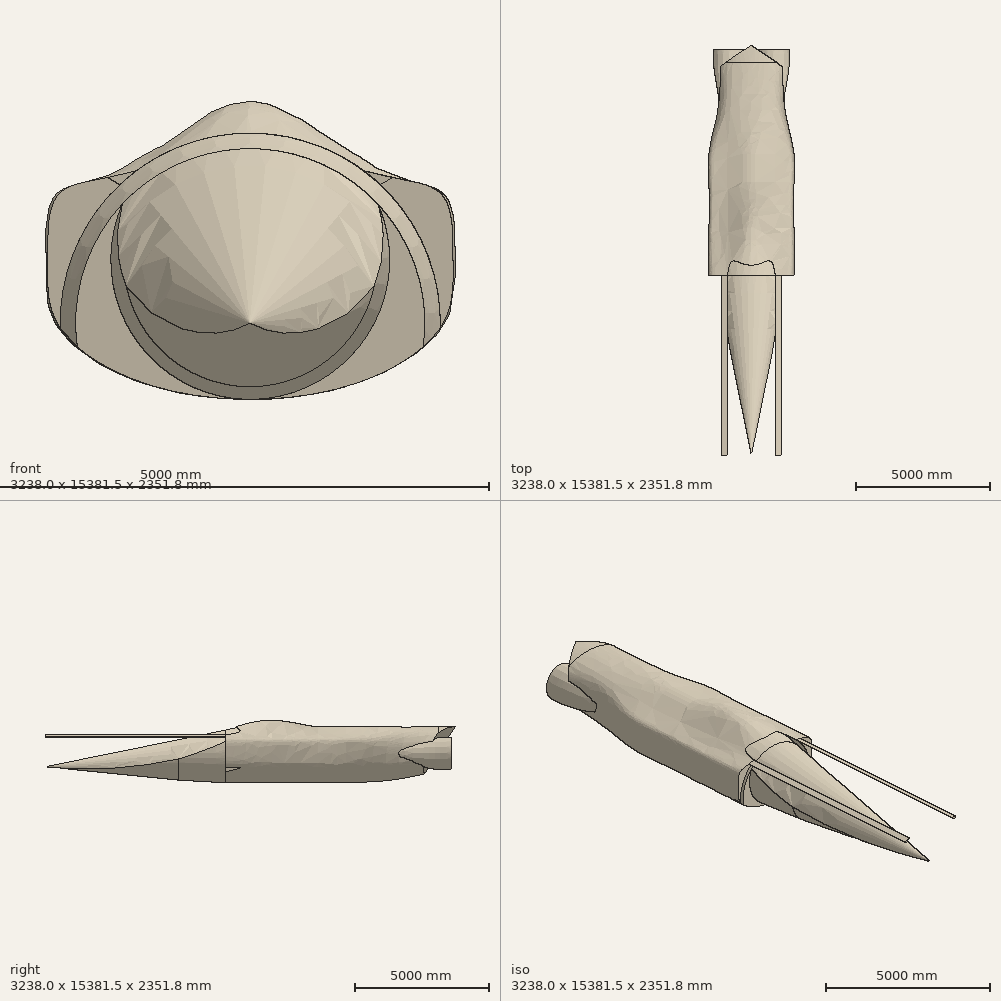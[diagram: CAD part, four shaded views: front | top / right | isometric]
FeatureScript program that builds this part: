
annotation { "Feature Type Name" : "Feature", "Feature Type Description" : "" }
export const myFeature = defineFeature(function(context is Context, id is Id, definition is map)
    precondition{}
    {
        {
            var Q0;
            Q0=qCreatedBy(makeId("Front.planeOp"),FACE);
            cPlane(context, id + "F0", {"entities" : qUnion([Q0]), "cplaneType" : CPlaneType.OFFSET, "offset" : 1750 * mm, "width" : 152.4 * mm, "height" : 152.4 * mm});
        }
        {
            var Q0;
            Q0=qCreatedBy(id+"F0.planeOp",FACE);
            var sketch = newSketch(context, id + "F1", { "sketchPlane" : qUnion([Q0])});
            skPoint(sketch, "E0.middle", {"position": v(0, 0) * mm});
            skFitSpline(sketch, "E1", {"points": [v(0, 877.87) * mm, v(1060, 662.5) * mm, v(1517.6, 506.84) * mm, v(1600, 0) * mm, v(1517.6, -506.84) * mm, v(750, -1000) * mm, v(-750, -1000) * mm, v(-1517.6, -506.84) * mm, v(-1600, 0) * mm, v(-1517.6, 506.84) * mm, v(-1060, 662.5) * mm, v(0, 877.87) * mm]});
            skSolve(sketch);
        }
        {
            var Q0;
            Q0=qCreatedBy(makeId("Front.planeOp"),FACE);
            var sketch = newSketch(context, id + "F2", { "sketchPlane" : qUnion([Q0])});
            skPoint(sketch, "E2.middle", {"position": v(0, 0) * mm});
            skFitSpline(sketch, "E3", {"points": [v(0, 1250) * mm, v(1060, 662.5) * mm, v(1517.6, 506.84) * mm, v(1600, 0) * mm, v(1517.6, -506.84) * mm, v(750, -1000) * mm, v(-750, -1000) * mm, v(-1517.6, -506.84) * mm, v(-1600, 0) * mm, v(-1517.6, 506.84) * mm, v(-1060, 662.5) * mm, v(0, 1250) * mm]});
            skSolve(sketch);
        }
        {
            var Q0;
            Q0=qCreatedBy(makeId("Front.planeOp"),FACE);
            cPlane(context, id + "F3", {"entities" : qUnion([Q0]), "cplaneType" : CPlaneType.OFFSET, "offset" : 1750 * mm, "oppositeDirection" : true, "width" : 150 * mm, "height" : 150 * mm});
        }
        {
            var Q0;
            Q0=qCreatedBy(id+"F3.planeOp",FACE);
            var sketch = newSketch(context, id + "F4", { "sketchPlane" : qUnion([Q0])});
            skPoint(sketch, "E4.middle", {"position": v(0, 0) * mm});
            skFitSpline(sketch, "E5", {"points": [v(0, 1000) * mm, v(1060, 662.5) * mm, v(1517.6, 506.84) * mm, v(1600, 0) * mm, v(1517.6, -506.84) * mm, v(750, -1000) * mm, v(-750, -1000) * mm, v(-1517.6, -506.84) * mm, v(-1600, 0) * mm, v(-1517.6, 506.84) * mm, v(-1060, 662.5) * mm, v(0, 1000) * mm]});
            skSolve(sketch);
        }
        {
            var Q0;
            Q0=qCreatedBy(makeId("Front.planeOp"),FACE);
            cPlane(context, id + "F5", {"entities" : qUnion([Q0]), "cplaneType" : CPlaneType.OFFSET, "offset" : 2800 * mm, "oppositeDirection" : true, "width" : 150 * mm, "height" : 150 * mm});
        }
        {
            var Q0;
            Q0=qCreatedBy(id+"F5.planeOp",FACE);
            var sketch = newSketch(context, id + "F6", { "sketchPlane" : qUnion([Q0])});
            skPoint(sketch, "E6.middle", {"position": v(0, 0) * mm});
            skFitSpline(sketch, "E7", {"points": [v(0, 1000) * mm, v(1060, 662.5) * mm, v(1517.6, 506.84) * mm, v(1600, 0) * mm, v(1517.6, -506.84) * mm, v(750, -1000) * mm, v(-750, -1000) * mm, v(-1517.6, -506.84) * mm, v(-1600, 0) * mm, v(-1517.6, 506.84) * mm, v(-1060, 662.5) * mm, v(0, 1000) * mm]});
            skSolve(sketch);
        }
        {
            var Q0;
            Q0=qCreatedBy(makeId("Front.planeOp"),FACE);
            cPlane(context, id + "F7", {"entities" : qUnion([Q0]), "cplaneType" : CPlaneType.OFFSET, "offset" : 4500 * mm, "oppositeDirection" : true, "width" : 150 * mm, "height" : 150 * mm});
        }
        {
            var Q0;
            Q0=qCreatedBy(id+"F7.planeOp",FACE);
            var sketch = newSketch(context, id + "F8", { "sketchPlane" : qUnion([Q0])});
            skPoint(sketch, "E8.middle", {"position": v(0, 0) * mm});
            skFitSpline(sketch, "E9", {"points": [v(0, 1000) * mm, v(1060, 662.5) * mm, v(1250, 0) * mm, v(1060, -662.5) * mm, v(0, -1000) * mm, v(-1060, -662.5) * mm, v(-1250, 0) * mm, v(-1060, 662.5) * mm, v(0, 1000) * mm]});
            skSolve(sketch);
        }
        {
            var Q0;
            Q0=qCreatedBy(makeId("Front.planeOp"),FACE);
            cPlane(context, id + "F9", {"entities" : qUnion([Q0]), "cplaneType" : CPlaneType.OFFSET, "offset" : 6232.05 * mm, "oppositeDirection" : true, "width" : 150 * mm, "height" : 150 * mm});
        }
        {
            var Q0;
            Q0=qCreatedBy(id+"F9.planeOp",FACE);
            var sketch = newSketch(context, id + "F10", { "sketchPlane" : qUnion([Q0])});
            skPoint(sketch, "E10.middle", {"position": v(0, 0) * mm});
            skFitSpline(sketch, "E11", {"points": [v(0, 1000) * mm, v(1060, 662.5) * mm, v(1250, 0) * mm, v(848, -530) * mm, v(-848, -530) * mm, v(-1250, 0) * mm, v(-1060, 662.5) * mm, v(0, 1000) * mm]});
            skSolve(sketch);
        }
        {
            var Q0;
            Q0 = qSketchRegion(id + "F1", true);
            var Q1;
            Q1 = qSketchRegion(id + "F2", true);
            var Q2;
            Q2 = qSketchRegion(id + "F4", true);
            var Q3;
            Q3 = qSketchRegion(id + "F6", true);
            var Q4;
            Q4 = qSketchRegion(id + "F8", true);
            var Q5;
            Q5 = qSketchRegion(id + "F10", true);
            loft(context, id + "F11", {"sheetProfilesArray" : [{ "sheetProfileEntities" : qUnion([Q0]) }, { "sheetProfileEntities" : qUnion([Q1]) }, { "sheetProfileEntities" : qUnion([Q2]) }, { "sheetProfileEntities" : qUnion([Q3]) }, { "sheetProfileEntities" : qUnion([Q4]) }, { "sheetProfileEntities" : qUnion([Q5]) }]});
        }
        {
            var Q0;
            Q0=makeQuery(id+"F11.opLoft","CAP_FACE",FACE,{"disambiguationData":[OSD([makeQuery(id+"F10.imprint","IMPRINT",FACE,{"disambiguationData":[TD([[makeQuery(id+"F10.imprint","IMPRINT",EDGE,{"derivedFrom":sQuery(id+"F10.wireOp",EDGE,"E11")}),-1.0]])]})])],"isStart":true});
            extrude(context, id + "F12", {"entities" : qUnion([Q0]), "operationType" : NewBodyOperationType.ADD, "depth" : 649.4 * mm});
        }
        {
            var Q0;
            Q0=qCreatedBy(makeId("Right.planeOp"),FACE);
            var sketch = newSketch(context, id + "F13", { "sketchPlane" : qUnion([Q0])});
            skLineSegment(sketch, "E12", {"start": v(0, 0) * mm, "end": v(4500, 0) * mm});
            skLineSegment(sketch, "E13", {"start": v(4500, 0) * mm, "end": v(6232.05, 0) * mm});
            skLineSegment(sketch, "E14", {"start": v(4500, 0) * mm, "end": v(4500, 1000) * mm});
            skLineSegment(sketch, "E15", {"start": v(4500, 1000) * mm, "end": v(6881.46, 1000) * mm});
            skLineSegment(sketch, "E16", {"start": v(6881.46, 1000) * mm, "end": v(6881.46, -1000) * mm});
            skLineSegment(sketch, "E17", {"start": v(6881.46, 1000) * mm, "end": v(6232.05, 0) * mm});
            skLineSegment(sketch, "E18", {"start": v(6232.05, 0) * mm, "end": v(5582.64, -1000) * mm});
            skLineSegment(sketch, "E19", {"start": v(5582.64, -1000) * mm, "end": v(6881.46, -1000) * mm});
            skSolve(sketch);
        }
        {
            var Q0;
            Q0=makeQuery(id+"F13.imprint","IMPRINT",FACE,{"disambiguationData":[TD([[makeQuery(id+"F13.imprint","IMPRINT",EDGE,{"derivedFrom":sQuery(id+"F13.wireOp",EDGE,"E16")}),-1.0]])]});
            var Q1;
            Q1=sQuery(id+"F13.wireOp",EDGE,"E15");
            revolve(context, id + "F14", {"operationType" : NewBodyOperationType.REMOVE, "entities" : qUnion([Q0]), "axis" : qUnion([Q1]), "revolveType" : RevolveType.SYMMETRIC, "oppositeDirection" : true, "angle" : 182 * degree});
        }
        {
            var Q0;
            Q0=makeQuery(id+"F11.opLoft","CAP_FACE",FACE,{"disambiguationData":[OSD([makeQuery(id+"F1.imprint","IMPRINT",FACE,{"disambiguationData":[TD([[makeQuery(id+"F1.imprint","IMPRINT",EDGE,{"derivedFrom":sQuery(id+"F1.wireOp",EDGE,"E1")}),-1.0]])]})])],"isStart":true});
            extrude(context, id + "F15", {"entities" : qUnion([Q0]), "depth" : 6750 * mm});
        }
        {
            var Q0;
            Q0=qCreatedBy(makeId("Right.planeOp"),FACE);
            var sketch = newSketch(context, id + "F16", { "sketchPlane" : qUnion([Q0])});
            skLineSegment(sketch, "E20", {"start": v(0, 0) * mm, "end": v(-3500, 0) * mm});
            skLineSegment(sketch, "E21", {"start": v(-3500, 0) * mm, "end": v(-3500, -1000) * mm});
            skLineSegment(sketch, "E22", {"start": v(-3500, -1000) * mm, "end": v(-8500, -1000) * mm});
            skLineSegment(sketch, "E23", {"start": v(-8500, -1000) * mm, "end": v(-8500, -499.31) * mm});
            skLineSegment(sketch, "E24", {"start": v(-1151.4, 0) * mm, "end": v(-1151.4, 1000) * mm});
            skLineSegment(sketch, "E25", {"start": v(-1151.4, 1000) * mm, "end": v(-8500, -499.31) * mm});
            skLineSegment(sketch, "E26", {"start": v(-8500, -499.31) * mm, "end": v(-3500, -1000) * mm});
            skLineSegment(sketch, "E27", {"start": v(-1151.4, 1000) * mm, "end": v(-8500, 1000) * mm});
            skLineSegment(sketch, "E28", {"start": v(-8500, 1000) * mm, "end": v(-8500, -499.31) * mm});
            skLineSegment(sketch, "E29", {"start": v(-8500, -1000) * mm, "end": v(-8500, -1750) * mm});
            skLineSegment(sketch, "E30", {"start": v(-8500, -1750) * mm, "end": v(-1750, -1750) * mm});
            skPoint(sketch, "E30.endSnap0", {"position": v(-1750, 0) * mm});
            skLineSegment(sketch, "E31", {"start": v(-1750, 0) * mm, "end": v(-1750, -1099.92) * mm});
            skLineSegment(sketch, "E32", {"start": v(-1750, -1099.92) * mm, "end": v(-3500, -1000) * mm});
            skLineSegment(sketch, "E33", {"start": v(-1750, -1099.92) * mm, "end": v(-1750, -1750) * mm});
            skLineSegment(sketch, "E34", {"start": v(-8500, -499.31) * mm, "end": v(-3500, -499.31) * mm});
            skSolve(sketch);
        }
        {
            var Q0;
            Q0=makeQuery(id+"F16.imprint","IMPRINT",FACE,{"disambiguationData":[TD([[makeQuery(id+"F16.imprint","IMPRINT",EDGE,{"derivedFrom":sQuery(id+"F16.wireOp",EDGE,"E25")}),-1.0]])]});
            var Q1;
            Q1=sQuery(id+"F16.wireOp",EDGE,"E34");
            revolve(context, id + "F17", {"operationType" : NewBodyOperationType.REMOVE, "entities" : qUnion([Q0]), "axis" : qUnion([Q1]), "revolveType" : RevolveType.SYMMETRIC, "oppositeDirection" : true, "angle" : 250 * degree});
        }
        {
            var Q0;
            Q0=makeQuery(id+"F16.imprint","IMPRINT",FACE,{"disambiguationData":[TD([[makeQuery(id+"F16.imprint","IMPRINT",EDGE,{"derivedFrom":sQuery(id+"F16.wireOp",EDGE,"E22")}),-1.0]])]});
            var Q1;
            Q1=makeQuery(id+"F16.imprint","IMPRINT",FACE,{"disambiguationData":[TD([[makeQuery(id+"F16.imprint","IMPRINT",EDGE,{"derivedFrom":sQuery(id+"F16.wireOp",EDGE,"E22")}),1.0]])]});
            var Q2;
            Q2=sQuery(id+"F16.wireOp",EDGE,"E20");
            revolve(context, id + "F18", {"operationType" : NewBodyOperationType.REMOVE, "entities" : qUnion([Q0, Q1]), "axis" : qUnion([Q2]), "revolveType" : RevolveType.SYMMETRIC, "angle" : 240 * degree});
        }
        {
            var Q0;
            Q0=qCreatedBy(makeId("Front.planeOp"),FACE);
            cPlane(context, id + "F19", {"entities" : qUnion([Q0]), "cplaneType" : CPlaneType.OFFSET, "offset" : 3500 * mm, "oppositeDirection" : true, "width" : 150 * mm, "height" : 150 * mm});
        }
        {
            var Q0;
            Q0=qCreatedBy(id+"F19.planeOp",FACE);
            var sketch = newSketch(context, id + "F20", { "sketchPlane" : qUnion([Q0])});
            skCircle(sketch, "E35", {"center": v(-825, 0) * mm, "radius": 600 * mm});
            skCircle(sketch, "E36", {"center": v(825, 0) * mm, "radius": 600 * mm});
            skSolve(sketch);
        }
        {
            var Q0;
            Q0=qCreatedBy(makeId("Front.planeOp"),FACE);
            cPlane(context, id + "F21", {"entities" : qUnion([Q0]), "cplaneType" : CPlaneType.OFFSET, "offset" : 4500 * mm, "oppositeDirection" : true, "width" : 150 * mm, "height" : 150 * mm});
        }
        {
            var Q0;
            Q0=qCreatedBy(id+"F21.planeOp",FACE);
            var sketch = newSketch(context, id + "F22", { "sketchPlane" : qUnion([Q0])});
            skCircle(sketch, "E37", {"center": v(-825, 0) * mm, "radius": 400 * mm});
            skCircle(sketch, "E38", {"center": v(825, 0) * mm, "radius": 400 * mm});
            skSolve(sketch);
        }
        {
            var Q0;
            Q0=qCreatedBy(makeId("Front.planeOp"),FACE);
            cPlane(context, id + "F23", {"entities" : qUnion([Q0]), "cplaneType" : CPlaneType.OFFSET, "offset" : 6232.05 * mm, "oppositeDirection" : true, "width" : 150 * mm, "height" : 150 * mm});
        }
        {
            var Q0;
            Q0=qCreatedBy(id+"F23.planeOp",FACE);
            var sketch = newSketch(context, id + "F24", { "sketchPlane" : qUnion([Q0])});
            skCircle(sketch, "E39", {"center": v(-825, 0) * mm, "radius": 600 * mm});
            skCircle(sketch, "E40", {"center": v(825, 0) * mm, "radius": 600 * mm});
            skSolve(sketch);
        }
        {
            var Q0;
            Q0=qCreatedBy(makeId("Front.planeOp"),FACE);
            cPlane(context, id + "F25", {"entities" : qUnion([Q0]), "cplaneType" : CPlaneType.OFFSET, "offset" : 6732.05 * mm, "oppositeDirection" : true, "width" : 150 * mm, "height" : 150 * mm});
        }
        {
            var Q0;
            Q0=qCreatedBy(id+"F25.planeOp",FACE);
            var sketch = newSketch(context, id + "F26", { "sketchPlane" : qUnion([Q0])});
            skCircle(sketch, "E41", {"center": v(-825, 0) * mm, "radius": 600 * mm});
            skCircle(sketch, "E42", {"center": v(825, 0) * mm, "radius": 600 * mm});
            skSolve(sketch);
        }
        {
            var Q0;
            Q0=makeQuery(id+"F20.imprint","IMPRINT",FACE,{"disambiguationData":[TD([[makeQuery(id+"F20.imprint","IMPRINT",EDGE,{"derivedFrom":sQuery(id+"F20.wireOp",EDGE,"E35")}),1.0]])]});
            var Q1;
            Q1=makeQuery(id+"F22.imprint","IMPRINT",FACE,{"disambiguationData":[TD([[makeQuery(id+"F22.imprint","IMPRINT",EDGE,{"derivedFrom":sQuery(id+"F22.wireOp",EDGE,"E37")}),1.0]])]});
            var Q2;
            Q2=makeQuery(id+"F24.imprint","IMPRINT",FACE,{"disambiguationData":[TD([[makeQuery(id+"F24.imprint","IMPRINT",EDGE,{"derivedFrom":sQuery(id+"F24.wireOp",EDGE,"E39")}),1.0]])]});
            var Q3;
            Q3=makeQuery(id+"F26.imprint","IMPRINT",FACE,{"disambiguationData":[TD([[makeQuery(id+"F26.imprint","IMPRINT",EDGE,{"derivedFrom":sQuery(id+"F26.wireOp",EDGE,"E41")}),1.0]])]});
            loft(context, id + "F27", {"sheetProfilesArray" : [{ "sheetProfileEntities" : qUnion([Q0]) }, { "sheetProfileEntities" : qUnion([Q1]) }, { "sheetProfileEntities" : qUnion([Q2]) }, { "sheetProfileEntities" : qUnion([Q3]) }]});
        }
        {
            var Q0;
            Q0=makeQuery(id+"F20.imprint","IMPRINT",FACE,{"disambiguationData":[TD([[makeQuery(id+"F20.imprint","IMPRINT",EDGE,{"derivedFrom":sQuery(id+"F20.wireOp",EDGE,"E36")}),1.0]])]});
            var Q1;
            Q1=makeQuery(id+"F22.imprint","IMPRINT",FACE,{"disambiguationData":[TD([[makeQuery(id+"F22.imprint","IMPRINT",EDGE,{"derivedFrom":sQuery(id+"F22.wireOp",EDGE,"E38")}),1.0]])]});
            var Q2;
            Q2=makeQuery(id+"F24.imprint","IMPRINT",FACE,{"disambiguationData":[TD([[makeQuery(id+"F24.imprint","IMPRINT",EDGE,{"derivedFrom":sQuery(id+"F24.wireOp",EDGE,"E40")}),1.0]])]});
            var Q3;
            Q3=makeQuery(id+"F26.imprint","IMPRINT",FACE,{"disambiguationData":[TD([[makeQuery(id+"F26.imprint","IMPRINT",EDGE,{"derivedFrom":sQuery(id+"F26.wireOp",EDGE,"E42")}),1.0]])]});
            loft(context, id + "F28", {"sheetProfilesArray" : [{ "sheetProfileEntities" : qUnion([Q0]) }, { "sheetProfileEntities" : qUnion([Q1]) }, { "sheetProfileEntities" : qUnion([Q2]) }, { "sheetProfileEntities" : qUnion([Q3]) }]});
        }
    });
